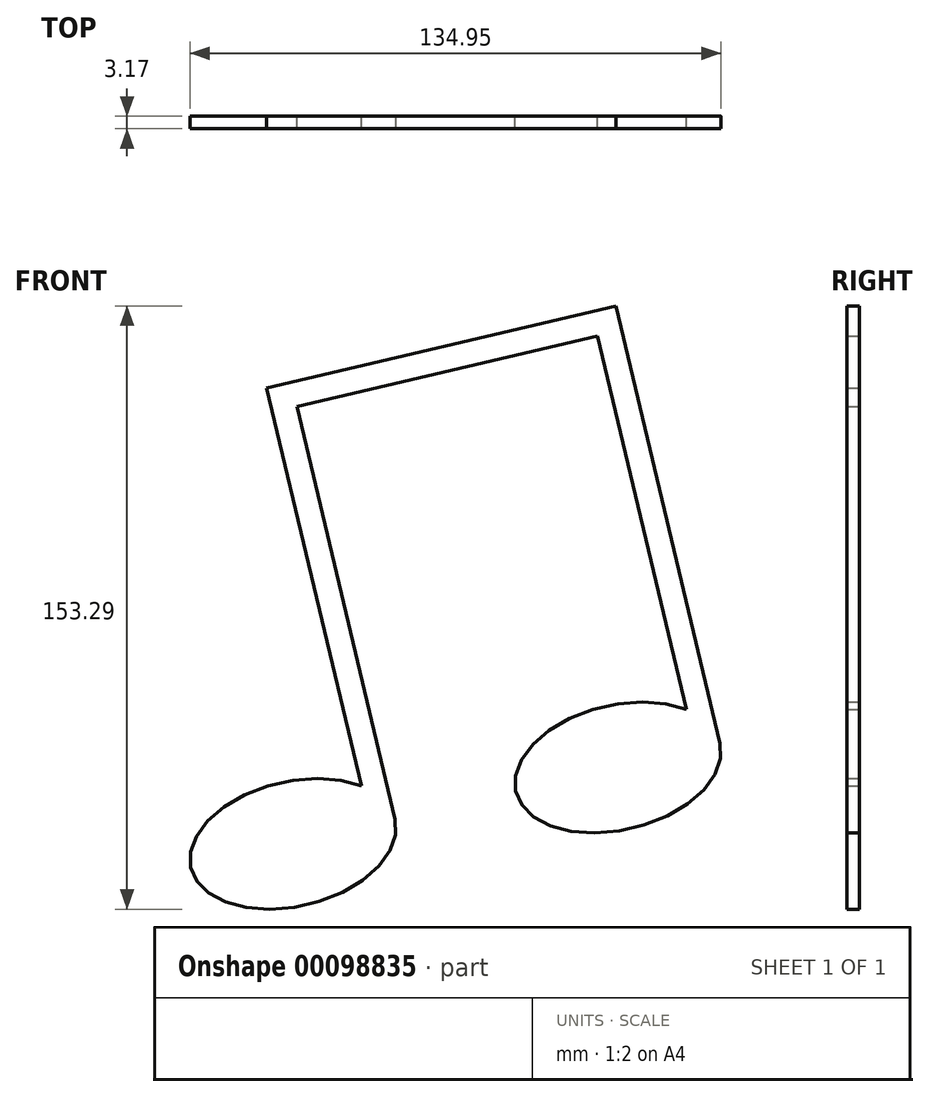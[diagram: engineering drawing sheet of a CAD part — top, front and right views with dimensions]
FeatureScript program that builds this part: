
annotation { "Feature Type Name" : "Feature", "Feature Type Description" : "" }
export const myFeature = defineFeature(function(context is Context, id is Id, definition is map)
    precondition{}
    {
        {
            var Q0;
            Q0=qCreatedBy(makeId("Front.planeOp"),FACE);
            var sketch = newSketch(context, id + "F0", { "sketchPlane" : qUnion([Q0])});
            skEllipticalArc(sketch, "E0", {});
            skLineSegment(sketch, "E1", {"start": v(-6.7, 115.84) * mm, "end": v(17.39, 14.7) * mm});
            skEllipticalArc(sketch, "E2", {});
            skLineSegment(sketch, "E3", {"start": v(108.5, 25.56) * mm, "end": v(82.04, 136.66) * mm});
            skLineSegment(sketch, "E4", {"start": v(-6.7, 115.84) * mm, "end": v(82.04, 136.66) * mm});
            skLineSegment(sketch, "E5", {"start": v(25.94, 6.18) * mm, "end": v(0.96, 111.1) * mm});
            skLineSegment(sketch, "E6", {"start": v(0.96, 111.1) * mm, "end": v(77.33, 129.04) * mm});
            skLineSegment(sketch, "E7", {"start": v(77.33, 129.04) * mm, "end": v(99.94, 34.09) * mm});
            const initialGuessF0  = {"E0": [0, 0, -0.9728012308245748, -0.23164145852198462, 0.02667, 0.015875, 3.8461400720426373, 3.1415926535897927], "E2": [0.08255, 0.01937778668326974, -0.9728012308245747, -0.23164145852198514, 0.02667, 0.015875, 3.846140072042637, 3.141592653589793]};
            skSetInitialGuess(sketch, initialGuessF0);
            skSolve(sketch);
        }
        {
            var Q0;
            Q0 = qSketchRegion(id + "F0", true);
            extrude(context, id + "F1", {"entities" : qUnion([Q0]), "depth" : 3.17 * mm});
        }
    });
